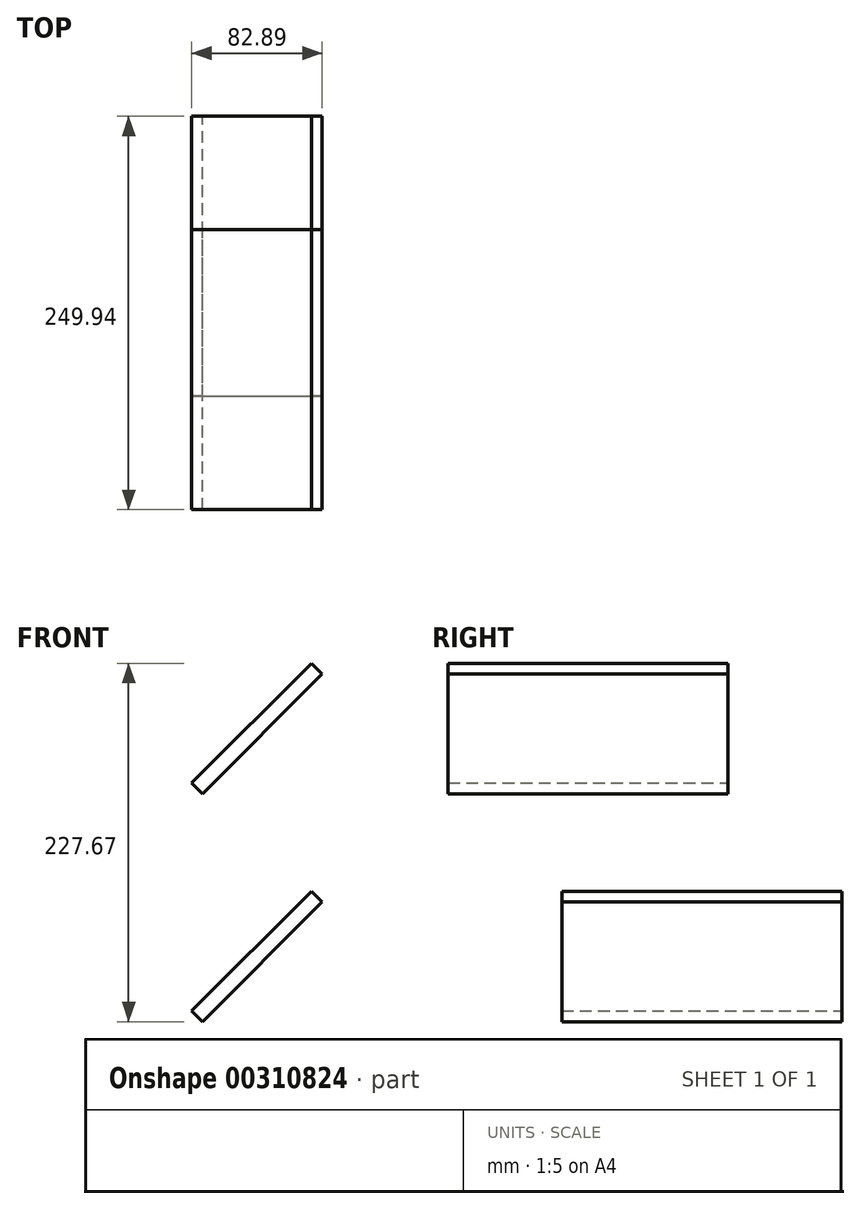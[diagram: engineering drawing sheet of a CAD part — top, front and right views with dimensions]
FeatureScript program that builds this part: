
annotation { "Feature Type Name" : "Feature", "Feature Type Description" : "" }
export const myFeature = defineFeature(function(context is Context, id is Id, definition is map)
    precondition{}
    {
        {
            var Q0;
            Q0=qCreatedBy(makeId("Front.planeOp"),FACE);
            var sketch = newSketch(context, id + "F0", { "sketchPlane" : qUnion([Q0])});
            skLineSegment(sketch, "E0.bottom", {"start": v(-30.26, 17.13) * mm, "end": v(-39.79, 17.13) * mm});
            skLineSegment(sketch, "E0.top", {"start": v(-30.26, 124.83) * mm, "end": v(-39.79, 124.83) * mm});
            skLineSegment(sketch, "E0.left", {"start": v(-30.26, 17.13) * mm, "end": v(-30.26, 124.83) * mm});
            skLineSegment(sketch, "E0.right", {"start": v(-39.79, 17.13) * mm, "end": v(-39.79, 124.83) * mm});
            skPoint(sketch, "E0.middle", {"position": v(-35.03, 70.98) * mm});
            skSolve(sketch);
        }
        {
            var Q0;
            Q0=makeQuery(id+"F0.imprint","IMPRINT",FACE,{"disambiguationData":[TD([[makeQuery(id+"F0.imprint","IMPRINT",EDGE,{"derivedFrom":sQuery(id+"F0.wireOp",EDGE,"E0.bottom")}),-1.0]])]});
            extrude(context, id + "F1", {"entities" : qUnion([Q0]), "depth" : 177.8 * mm});
        }
        {
            var Q0;
            Q0=makeQuery(id+"F1.opExtrude","SWEPT_BODY",BODY,{"disambiguationData":[OSD([sQuery(id+"F0.wireOp",EDGE,"E0.bottom"),sQuery(id+"F0.wireOp",EDGE,"E0.top"),sQuery(id+"F0.wireOp",EDGE,"E0.left"),sQuery(id+"F0.wireOp",EDGE,"E0.right")])]});
            var Q1;
            Q1=makeQuery(id+"F1.opExtrude","SWEPT_EDGE",EDGE,{"disambiguationData":[OSD([sQuery(id+"F0.wireOp",EDGE,"E0.bottom"),sQuery(id+"F0.wireOp",EDGE,"E0.left")])]});
            transform(context, id + "F2", {"entities" : qUnion([Q0]), "transformType" : TransformType.ROTATION, "transformAxis" : qUnion([Q1]), "angle" : 45 * degree, "makeCopy" : false});
        }
        {
            var Q0;
            Q0=makeQuery(id+"F1.opExtrude","SWEPT_BODY",BODY,{"disambiguationData":[OSD([sQuery(id+"F0.wireOp",EDGE,"E0.bottom"),sQuery(id+"F0.wireOp",EDGE,"E0.top"),sQuery(id+"F0.wireOp",EDGE,"E0.left"),sQuery(id+"F0.wireOp",EDGE,"E0.right")])]});
            transform(context, id + "F3", {"entities" : qUnion([Q0]), "transformType" : TransformType.TRANSLATION_3D, "dx" : 0 * mm, "dy" : 72.14 * mm, "dz" : -144.78 * mm, "makeCopy" : true});
        }
    });
